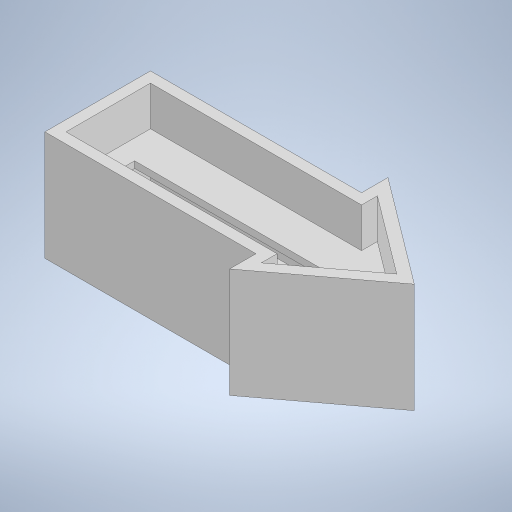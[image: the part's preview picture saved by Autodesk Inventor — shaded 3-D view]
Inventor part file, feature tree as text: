
AUTODESK INVENTOR PART (.ipt)
format: ipt  version: 2023 (Build 270158000, 158)  size: 302,592 bytes
history: native  units: in
note: dims shown in document units (in); Inventor stores cm internally (conversion verified against a paired STEP export)
features: sketch x9, extrude x4, projected_geometry x4, other x3, plane x1
ambient origin geometry x8: Origin, YZ Plane, XZ Plane, XY Plane, X Axis, Y Axis, Z Axis, Center Point
bodies: Solid1 (feature_tree)
feature tree (21):
  other  "Part_5_ledholder.ipt"
  extrude  "Extrusion1"  Depth=1.0in TaperAngle=0.0deg
  extrude  "Extrusion2"  Depth=0.1in
  extrude  "Extrusion3"  Depth=0.75in TaperAngle=0.0deg
  plane  "Work Plane1"
  extrude  "Extrusion4"  Depth=2.625in TaperAngle=0.0deg
  other  "Solid1::Part_5_ledholder.ipt"
  other  "TaggingFeature1"
  sketch  "Sketch1"  dims[d0=0.3937in d1=1.0in d2=0.0in]
  sketch  "Sketch2"  dims[d3=0.6in d4=0.0in d5=0.1in]
  sketch  "Sketch3"  dims[d6=0.0in d7=0.75in d8=0.0in]
  sketch  "Sketch4"  dims[d9=1.0625in d10=2.625in d11=0.0in]
  sketch  "Sketch6"
  sketch  "Sketch7"
  projected_geometry  "Projected Loop1"
  sketch  "Sketch8"
  projected_geometry  "Projected Loop2"
  sketch  "Sketch9"
  sketch  "Sketch10"
  projected_geometry  "Projected Loop3"
  projected_geometry  "Projected Loop4"
